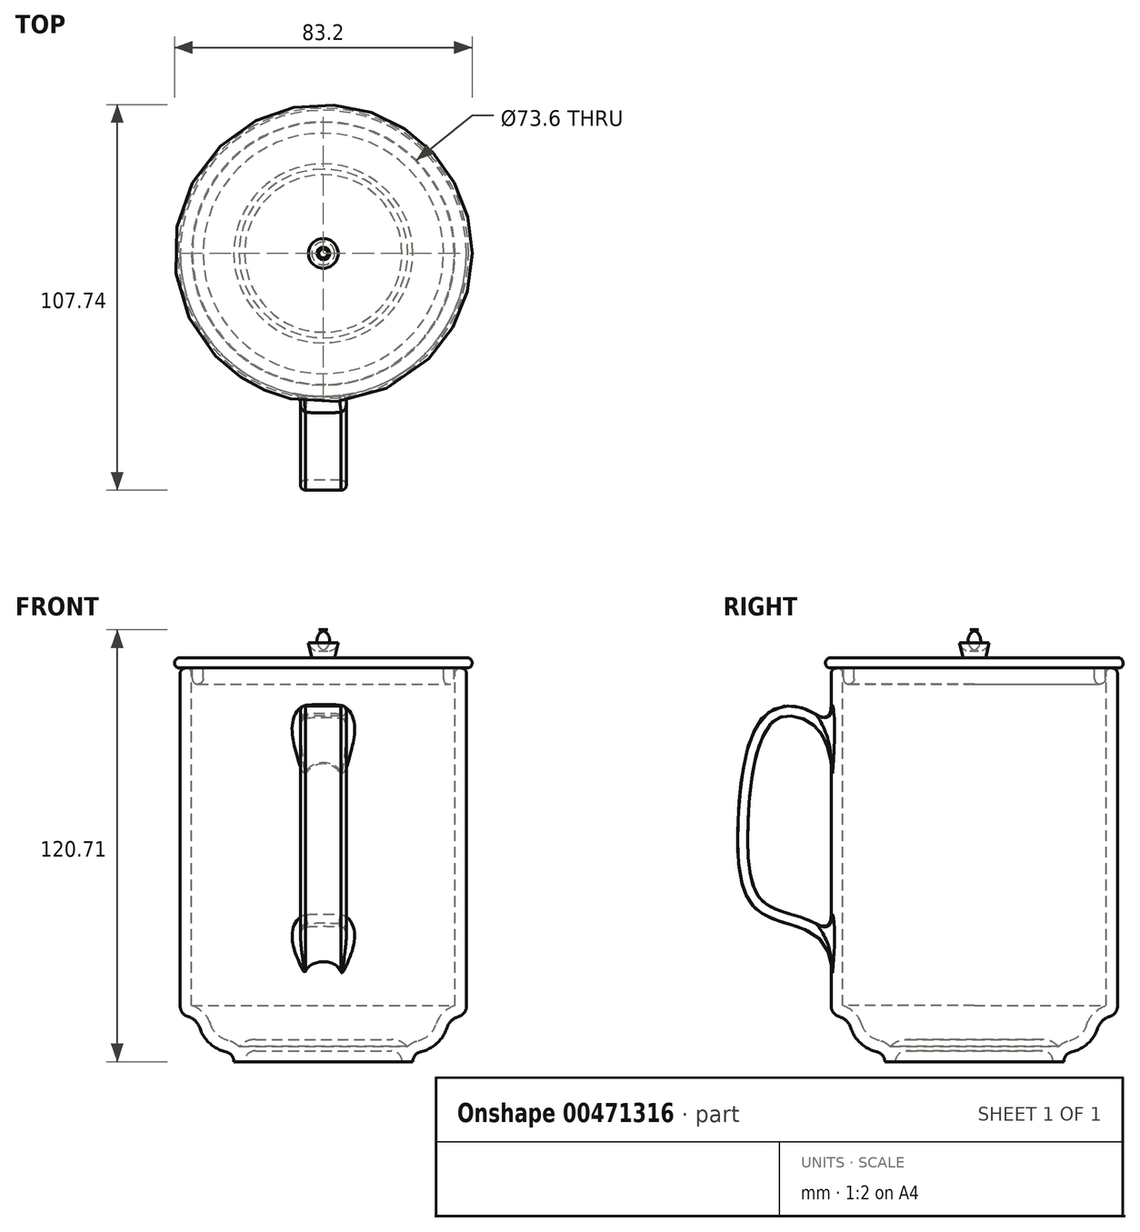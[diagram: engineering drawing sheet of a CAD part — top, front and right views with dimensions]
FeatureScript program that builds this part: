
annotation { "Feature Type Name" : "Feature", "Feature Type Description" : "" }
export const myFeature = defineFeature(function(context is Context, id is Id, definition is map)
    precondition{}
    {
        {
            var Q0;
            Q0=qCreatedBy(makeId("Front.planeOp"),FACE);
            var sketch = newSketch(context, id + "F0", { "sketchPlane" : qUnion([Q0])});
            skLineSegment(sketch, "E0", {"start": v(0, 0) * mm, "end": v(-25, 0) * mm});
            skLineSegment(sketch, "E1", {"start": v(-25, 0) * mm, "end": v(-25, 2.5) * mm});
            skLineSegment(sketch, "E2", {"start": v(-35, 12.5) * mm, "end": v(-40, 12.5) * mm});
            skLineSegment(sketch, "E3", {"start": v(-40, 12.5) * mm, "end": v(-40, 110) * mm});
            skArc(sketch, "E4", {"start": v(-35, 12.5) * mm, "mid": v(-32.07, 5.43) * mm, "end": v(-25, 2.5) * mm});
            skLineSegment(sketch, "E5", {"start": v(-40, 110) * mm, "end": v(0, 110) * mm});
            skLineSegment(sketch, "E6", {"start": v(0, 110) * mm, "end": v(0, 0) * mm});
            skSolve(sketch);
        }
        {
            var Q0;
            Q0 = qSketchRegion(id + "F0", true);
            var Q1;
            Q1=sQuery(id+"F0.wireOp",EDGE,"E6");
            revolve(context, id + "F1", {"entities" : qUnion([Q0]), "axis" : qUnion([Q1]), "revolveType" : RevolveType.FULL});
        }
        {
            var Q0;
            Q0=makeQuery(id+"F1.opRevolve","SWEPT_EDGE",EDGE,{"disambiguationData":[OSD([sQuery(id+"F0.wireOp",EDGE,"E2"),sQuery(id+"F0.wireOp",EDGE,"E3")])]});
            fillet(context, id + "F2", {"entities" : qUnion([Q0]), "radius" : 3 * mm, "tangentPropagation" : true, "allowEdgeOverflow" : false});
        }
        {
            var Q0;
            Q0=makeQuery(id+"F1.opRevolve","SWEPT_EDGE",EDGE,{"disambiguationData":[OSD([sQuery(id+"F0.wireOp",EDGE,"E2"),sQuery(id+"F0.wireOp",EDGE,"E4")])]});
            fillet(context, id + "F3", {"entities" : qUnion([Q0]), "radius" : 5 * mm, "tangentPropagation" : true, "allowEdgeOverflow" : false});
        }
        {
            var Q0;
            Q0=makeQuery(id+"F1.opRevolve","SWEPT_EDGE",EDGE,{"disambiguationData":[OSD([sQuery(id+"F0.wireOp",EDGE,"E1"),sQuery(id+"F0.wireOp",EDGE,"E4")])]});
            fillet(context, id + "F4", {"entities" : qUnion([Q0]), "radius" : 2.9 * mm, "tangentPropagation" : true, "allowEdgeOverflow" : false});
        }
        {
            var Q0;
            Q0=makeQuery(id+"F1.opRevolve","SWEPT_FACE",FACE,{"disambiguationData":[OSD([sQuery(id+"F0.wireOp",EDGE,"E0")])]});
            var sketch = newSketch(context, id + "F5", { "sketchPlane" : qUnion([Q0])});
            skCircle(sketch, "E7", {"center": v(0, 0) * mm, "radius": 22 * mm});
            skSolve(sketch);
        }
        {
            var Q0;
            Q0=makeQuery(id+"F5.imprint","IMPRINT",FACE,{"disambiguationData":[TD([[makeQuery(id+"F5.imprint","IMPRINT",EDGE,{"derivedFrom":sQuery(id+"F5.wireOp",EDGE,"E7")}),1.0]])]});
            extrude(context, id + "F6", {"entities" : qUnion([Q0]), "operationType" : NewBodyOperationType.REMOVE, "oppositeDirection" : true, "depth" : 3 * mm});
        }
        {
            var Q0;
            Q0=makeQuery(id+"F6.boolean.opBoolean","COPY",EDGE,{"derivedFrom":makeQuery(id+"F6.opExtrude","CAP_EDGE",EDGE,{"disambiguationData":[OSD([sQuery(id+"F5.wireOp",EDGE,"E7")])],"isStart":false})});
            fillet(context, id + "F7", {"entities" : qUnion([Q0]), "radius" : 3 * mm, "tangentPropagation" : true, "allowEdgeOverflow" : false});
        }
        {
            var Q0;
            Q0=makeQuery(id+"F1.opRevolve","SWEPT_FACE",FACE,{"disambiguationData":[OSD([sQuery(id+"F0.wireOp",EDGE,"E5")])]});
            shell(context, id + "F8", {"entities" : qUnion([Q0]), "thickness" : 3.2 * mm});
        }
        {
            var Q0;
            Q0=makeQuery(id+"F1.opRevolve","SWEPT_EDGE",EDGE,{"disambiguationData":[OSD([sQuery(id+"F0.wireOp",EDGE,"E3"),sQuery(id+"F0.wireOp",EDGE,"E5")])]});
            var Q1;
            Q1=makeQuery(id+"F8.opShell","OFFSET_EDGE",EDGE,{"disambiguationData":[OSD([sQuery(id+"F0.wireOp",EDGE,"E3"),sQuery(id+"F0.wireOp",EDGE,"E5")])]});
            fillet(context, id + "F9", {"entities" : qUnion([Q0, Q1]), "radius" : 1.5 * mm, "tangentPropagation" : true, "allowEdgeOverflow" : false});
        }
        {
            var Q0;
            Q0=qCreatedBy(makeId("Right.planeOp"),FACE);
            var sketch = newSketch(context, id + "F10", { "sketchPlane" : qUnion([Q0])});
            skFitSpline(sketch, "E8", {"points": [v(-38.27, 80.75) * mm, v(-42.85, 94.04) * mm, v(-56.32, 96.8) * mm, v(-64.58, 68.18) * mm, v(-61.6, 45.51) * mm, v(-51.84, 39.9) * mm, v(-38.25, 23.96) * mm], "startDerivative": vector(-8.29, 83.84) * mm, "endDerivative": vector(1, -207.18) * mm});
            skSolve(sketch);
        }
        {
            var Q0;
            Q0=sQuery(id+"F10.wireOp",EDGE,"E8");
            var Q1;
            Q1=sQuery(id+"F10.wireOp",VERTEX,"E8.start");
            cPlane(context, id + "F11", {"entities" : qUnion([Q0, Q1]), "cplaneType" : CPlaneType.CURVE_POINT, "offset" : 0 * mm, "width" : 150 * mm, "height" : 150 * mm});
        }
        {
            var Q0;
            Q0=qCreatedBy(id+"F11.planeOp",FACE);
            var sketch = newSketch(context, id + "F12", { "sketchPlane" : qUnion([Q0])});
            skLineSegment(sketch, "E9.bottom", {"start": v(4.97, -28.74) * mm, "end": v(-5.03, -28.74) * mm});
            skLineSegment(sketch, "E9.top", {"start": v(5.03, -31.54) * mm, "end": v(-4.97, -31.54) * mm});
            skPoint(sketch, "E9.middle", {"position": v(0, -30.14) * mm});
            skArc(sketch, "E10", {"start": v(-5.03, -28.74) * mm, "mid": v(-6.37, -30.17) * mm, "end": v(-4.97, -31.54) * mm});
            skArc(sketch, "E11", {"start": v(5.03, -31.54) * mm, "mid": v(6.43, -30.11) * mm, "end": v(4.97, -28.74) * mm});
            skSolve(sketch);
        }
        {
            var Q0;
            Q0=makeQuery(id+"F12.imprint","IMPRINT",FACE,{"disambiguationData":[TD([[makeQuery(id+"F12.imprint","IMPRINT",EDGE,{"derivedFrom":sQuery(id+"F12.wireOp",EDGE,"E9.bottom")}),1.0]])]});
            var Q1;
            Q1=sQuery(id+"F10.wireOp",EDGE,"E8");
            sweep(context, id + "F13", {"operationType" : NewBodyOperationType.ADD, "profiles" : qUnion([Q0]), "path" : qUnion([Q1])});
        }
        {
            var Q0;
            Q0=makeQuery(id+"F13.boolean.opBoolean","INTERSECT",EDGE,{"disambiguationData":[OD(1.0)],"derivedFrom":[makeQuery(id+"F1.opRevolve","SWEPT_FACE",FACE,{"disambiguationData":[OSD([sQuery(id+"F0.wireOp",EDGE,"E3")])]}),makeQuery(id+"F13.opSweep","SWEPT_FACE",FACE,{"disambiguationData":[OSD([sQuery(id+"F10.wireOp",EDGE,"E8"),sQuery(id+"F12.wireOp",EDGE,"E9.bottom")])]})]});
            var Q1;
            Q1=makeQuery(id+"F13.boolean.opBoolean","INTERSECT",EDGE,{"disambiguationData":[OD(0.0)],"derivedFrom":[makeQuery(id+"F1.opRevolve","SWEPT_FACE",FACE,{"disambiguationData":[OSD([sQuery(id+"F0.wireOp",EDGE,"E3")])]}),makeQuery(id+"F13.opSweep","SWEPT_FACE",FACE,{"disambiguationData":[OSD([sQuery(id+"F10.wireOp",EDGE,"E8"),sQuery(id+"F12.wireOp",EDGE,"E9.top")])]})]});
            fillet(context, id + "F14", {"entities" : qUnion([Q0, Q1]), "radius" : 3 * mm, "tangentPropagation" : true, "rho" : 0.5, "crossSection" : FilletCrossSection.CONIC, "allowEdgeOverflow" : false});
        }
        {
            var Q0;
            Q0=qCreatedBy(makeId("Front.planeOp"),FACE);
            var sketch = newSketch(context, id + "F15", { "sketchPlane" : qUnion([Q0])});
            skLineSegment(sketch, "E12", {"start": v(0, 110) * mm, "end": v(-40.6, 110) * mm});
            skLineSegment(sketch, "E13", {"start": v(-40.1, 112.91) * mm, "end": v(-3.2, 112.91) * mm});
            skLineSegment(sketch, "E14", {"start": v(-3.2, 112.91) * mm, "end": v(-4.15, 117.03) * mm});
            skLineSegment(sketch, "E15", {"start": v(-1.23, 120.7) * mm, "end": v(0, 120.7) * mm});
            skLineSegment(sketch, "E16", {"start": v(0, 120.7) * mm, "end": v(0, 110) * mm});
            skArc(sketch, "E17", {"start": v(-40.1, 112.91) * mm, "mid": v(-41.58, 111.67) * mm, "end": v(-40.6, 110) * mm});
            skPoint(sketch, "E18.visualSharp", {"position": v(-5, 120.7) * mm});
            skArc(sketch, "E18.filletArc", {"start": v(-1.23, 120.7) * mm, "mid": v(-3.58, 119.58) * mm, "end": v(-4.15, 117.03) * mm});
            skLineSegment(sketch, "E19", {"start": v(-36.6, 110) * mm, "end": v(-36.6, 107) * mm});
            skLineSegment(sketch, "E20", {"start": v(-33.6, 107) * mm, "end": v(-33.6, 110) * mm});
            skArc(sketch, "E21", {"start": v(-36.6, 107) * mm, "mid": v(-35.1, 105.5) * mm, "end": v(-33.6, 107) * mm});
            skSolve(sketch);
        }
        {
            var Q0;
            {var subQ0=sQuery(id+"F15.wireOp",EDGE,"E19");Q0=makeQuery(id+"F15.imprint","IMPRINT",FACE,{"disambiguationData":[TD([[makeQuery(id+"F15.imprint","IMPRINT",EDGE,{"derivedFrom":subQ0}),1.0]])]});}
            var Q1;
            Q1=makeQuery(id+"F15.imprint","IMPRINT",FACE,{"disambiguationData":[TD([[makeQuery(id+"F15.imprint","IMPRINT",EDGE,{"derivedFrom":sQuery(id+"F15.wireOp",EDGE,"E13")}),-1.0]])]});
            var Q2;
            Q2=sQuery(id+"F15.wireOp",EDGE,"E16");
            revolve(context, id + "F16", {"entities" : qUnion([Q0, Q1]), "axis" : qUnion([Q2]), "revolveType" : RevolveType.FULL});
        }
    });
